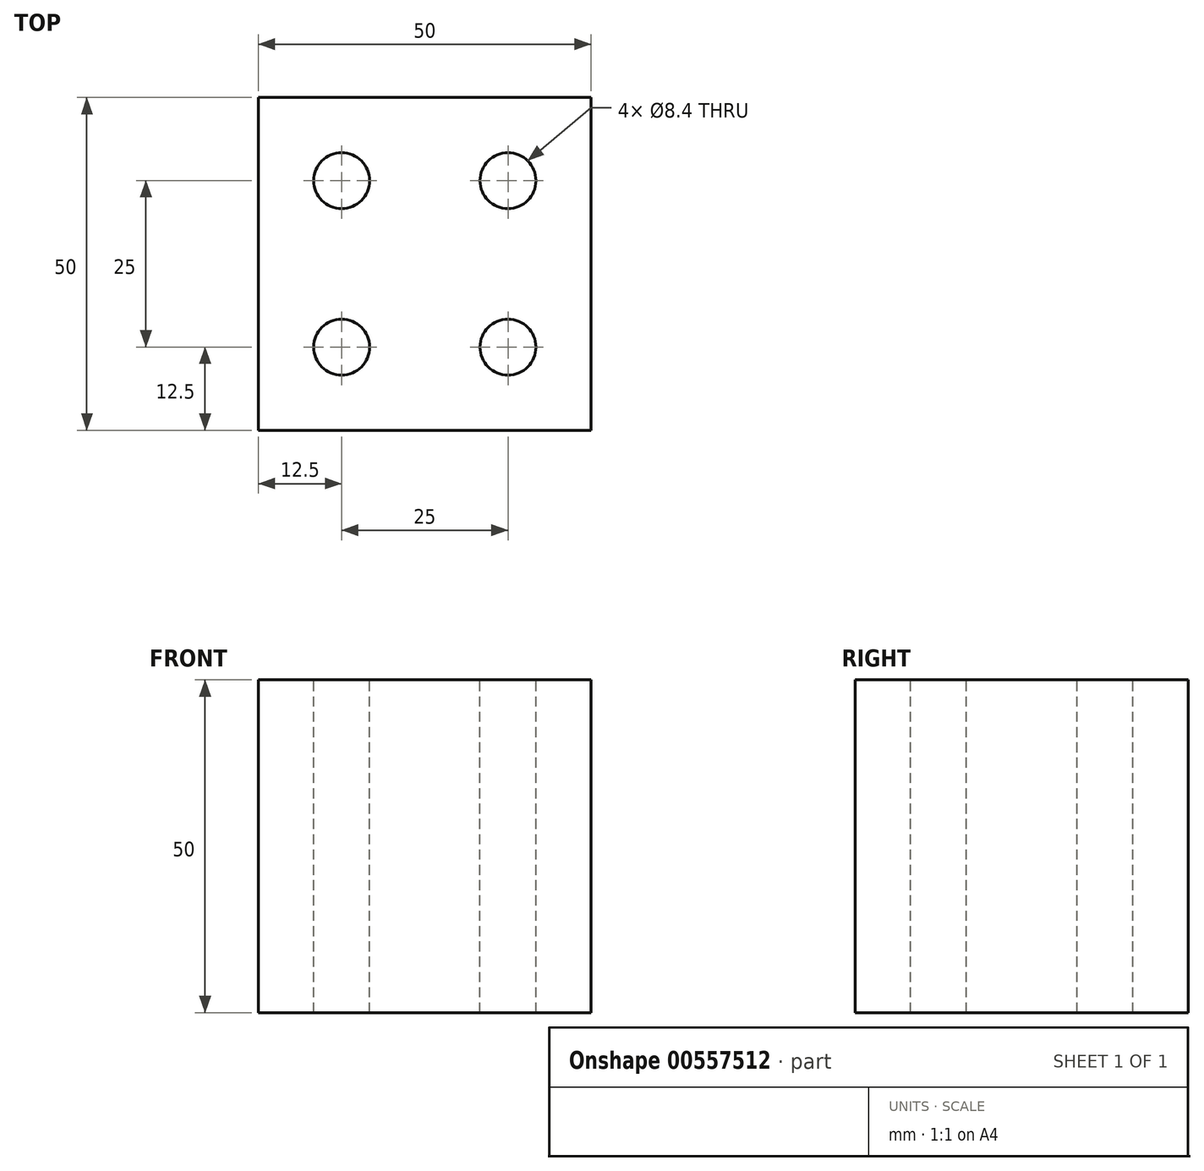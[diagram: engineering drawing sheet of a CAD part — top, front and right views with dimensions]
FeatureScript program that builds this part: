
annotation { "Feature Type Name" : "Feature", "Feature Type Description" : "" }
export const myFeature = defineFeature(function(context is Context, id is Id, definition is map)
    precondition{}
    {
        {
            var Q0;
            Q0=qCreatedBy(makeId("Front.planeOp"),FACE);
            var sketch = newSketch(context, id + "F0", { "sketchPlane" : qUnion([Q0])});
            skLineSegment(sketch, "E0.bottom", {"start": v(25, -25) * mm, "end": v(-25, -25) * mm});
            skLineSegment(sketch, "E0.top", {"start": v(25, 25) * mm, "end": v(-25, 25) * mm});
            skLineSegment(sketch, "E0.left", {"start": v(25, -25) * mm, "end": v(25, 25) * mm});
            skLineSegment(sketch, "E0.right", {"start": v(-25, -25) * mm, "end": v(-25, 25) * mm});
            skPoint(sketch, "E0.middle", {"position": v(0, 0) * mm});
            skSolve(sketch);
        }
        {
            var Q0;
            Q0=makeQuery(id+"F0.imprint","IMPRINT",FACE,{"disambiguationData":[TD([[makeQuery(id+"F0.imprint","IMPRINT",EDGE,{"derivedFrom":sQuery(id+"F0.wireOp",EDGE,"E0.bottom")}),-1.0]])]});
            extrude(context, id + "F1", {"entities" : qUnion([Q0]), "endBound" : BoundingType.SYMMETRIC, "depth" : 50 * mm, "offsetDistance" : 25.4 * mm});
        }
        {
            var Q0;
            Q0=makeQuery(id+"F1.opExtrude","SWEPT_FACE",FACE,{"disambiguationData":[OSD([sQuery(id+"F0.wireOp",EDGE,"E0.top")])]});
            var sketch = newSketch(context, id + "F2", { "sketchPlane" : qUnion([Q0])});
            skLineSegment(sketch, "E1.bottom", {"start": v(12.5, -12.5) * mm, "end": v(-12.5, -12.5) * mm});
            skLineSegment(sketch, "E1.top", {"start": v(12.5, 12.5) * mm, "end": v(-12.5, 12.5) * mm});
            skLineSegment(sketch, "E1.left", {"start": v(12.5, -12.5) * mm, "end": v(12.5, 12.5) * mm});
            skLineSegment(sketch, "E1.right", {"start": v(-12.5, -12.5) * mm, "end": v(-12.5, 12.5) * mm});
            skPoint(sketch, "E1.middle", {"position": v(0, 0) * mm});
            skSolve(sketch);
        }
        {
            var Q0;
            Q0=sQuery(id+"F2.wireOp",VERTEX,"E1.top.end");
            var Q1;
            Q1=sQuery(id+"F2.wireOp",VERTEX,"E1.left.end");
            var Q2;
            Q2=sQuery(id+"F2.wireOp",VERTEX,"E1.left.start");
            var Q3;
            Q3=sQuery(id+"F2.wireOp",VERTEX,"E1.right.start");
            var Q4;
            Q4=makeQuery(id+"F1.opExtrude","SWEPT_BODY",BODY,{"disambiguationData":[OSD([sQuery(id+"F0.wireOp",EDGE,"E0.bottom"),sQuery(id+"F0.wireOp",EDGE,"E0.top"),sQuery(id+"F0.wireOp",EDGE,"E0.left"),sQuery(id+"F0.wireOp",EDGE,"E0.right")])]});
            hole(context, id + "F3", {"style" : HoleStyle.SIMPLE, "endStyle" : HoleEndStyle.THROUGH, "standardTappedOrClearance" : lookupTablePath({ "standard" : "ISO", "fit" : "Close", "size" : "M8", "type" : "Clearance" }), "standardBlindInLast" : lookupTablePath({ "fit" : "Close", "standard" : "ISO", "size" : "M8", "type" : "Clearance" }), "holeDiameter" : 8.4 * mm, "isTappedThrough" : true, "tappedDepth" : 12.7 * mm, "tapClearance" : 3, "locations" : qUnion([Q0, Q1, Q2, Q3]), "scope" : qUnion([Q4])});
        }
    });
